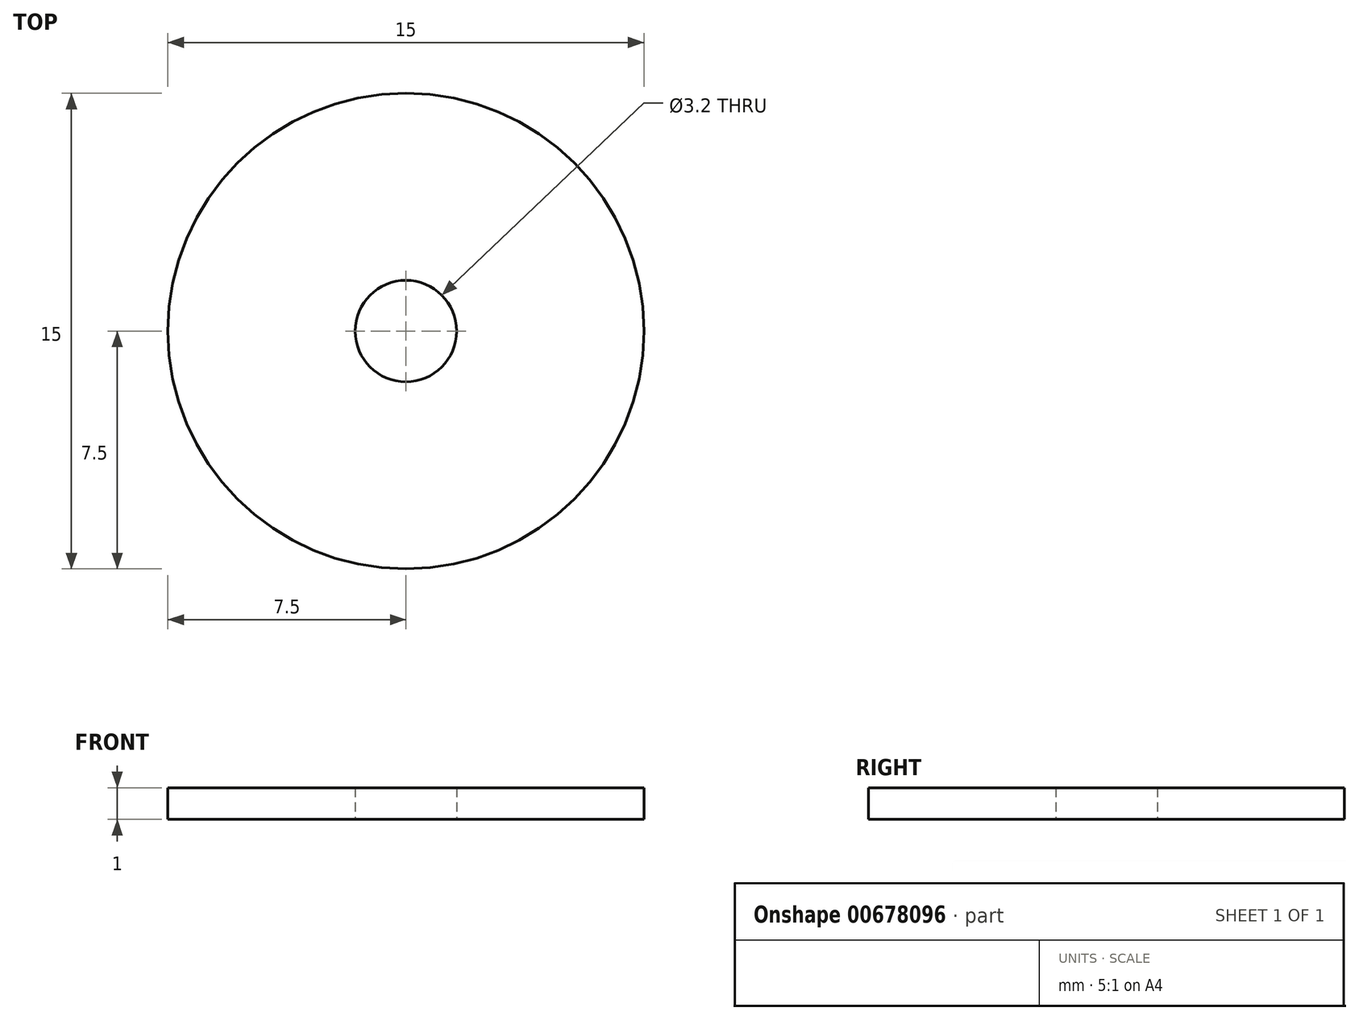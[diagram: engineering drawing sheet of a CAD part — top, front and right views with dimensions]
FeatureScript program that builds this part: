
annotation { "Feature Type Name" : "Feature", "Feature Type Description" : "" }
export const myFeature = defineFeature(function(context is Context, id is Id, definition is map)
    precondition{}
    {
        {
            var Q0;
            Q0=qCreatedBy(makeId("Top.planeOp"),FACE);
            var sketch = newSketch(context, id + "F0", { "sketchPlane" : qUnion([Q0])});
            skCircle(sketch, "E0", {"center": v(0, 0) * mm, "radius": 1.6 * mm});
            skCircle(sketch, "E1", {"center": v(0, 0) * mm, "radius": 7.5 * mm});
            skSolve(sketch);
        }
        {
            var Q0;
            Q0=makeQuery(id+"F0.imprint","IMPRINT",FACE,{"disambiguationData":[TD([[makeQuery(id+"F0.imprint","IMPRINT",EDGE,{"derivedFrom":sQuery(id+"F0.wireOp",EDGE,"E0")}),-1.0]])]});
            extrude(context, id + "F1", {"entities" : qUnion([Q0]), "depth" : 1 * mm, "offsetDistance" : 25 * mm});
        }
    });
